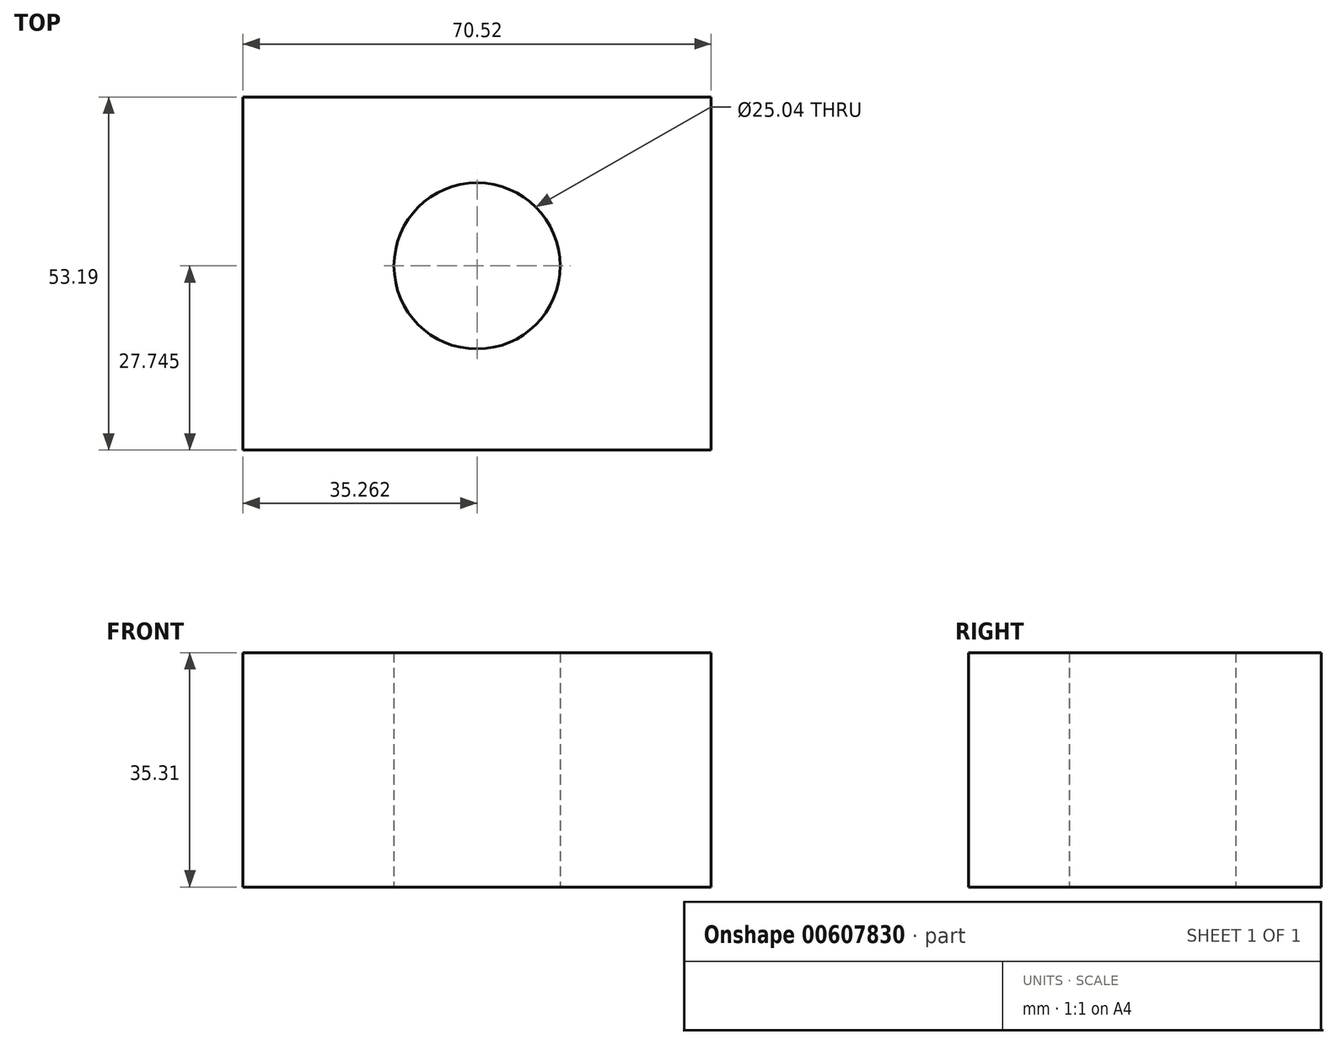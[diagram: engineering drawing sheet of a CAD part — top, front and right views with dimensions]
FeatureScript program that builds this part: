
annotation { "Feature Type Name" : "Feature", "Feature Type Description" : "" }
export const myFeature = defineFeature(function(context is Context, id is Id, definition is map)
    precondition{}
    {
        {
            var Q0;
            Q0=qCreatedBy(makeId("Top.planeOp"),FACE);
            var sketch = newSketch(context, id + "F0", { "sketchPlane" : qUnion([Q0])});
            skLineSegment(sketch, "E0.bottom", {"start": v(0, 0) * mm, "end": v(-70.52, 0) * mm});
            skLineSegment(sketch, "E0.top", {"start": v(0, 53.19) * mm, "end": v(-70.52, 53.19) * mm});
            skLineSegment(sketch, "E0.left", {"start": v(0, 0) * mm, "end": v(0, 53.19) * mm});
            skLineSegment(sketch, "E0.right", {"start": v(-70.52, 0) * mm, "end": v(-70.52, 53.19) * mm});
            skCircle(sketch, "E1", {"center": v(-35.26, 27.75) * mm, "radius": 12.52 * mm});
            skPoint(sketch, "E1.centerSnap0", {"position": v(-35.26, 53.19) * mm});
            skSolve(sketch);
        }
        {
            var Q0;
            Q0 = qSketchRegion(id + "F0", true);
            var Q1;
            Q1=makeQuery(id+"F0.imprint","IMPRINT",FACE,{"disambiguationData":[TD([[makeQuery(id+"F0.imprint","IMPRINT",EDGE,{"derivedFrom":sQuery(id+"F0.wireOp",EDGE,"E0.bottom")}),-1.0]])]});
            extrude(context, id + "F1", {"entities" : qUnion([Q0, Q1]), "depth" : 35.3 * mm, "offsetDistance" : 25.4 * mm});
        }
    });
